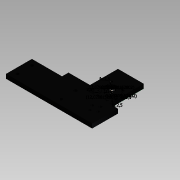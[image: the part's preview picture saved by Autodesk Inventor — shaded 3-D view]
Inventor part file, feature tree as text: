
AUTODESK INVENTOR PART (.ipt)
format: ipt  version: 2015 SP1 (Build 190203100, 203)  size: 229,888 bytes
history: native  units: mm
features: sketch x13, extrude x11, reference x5, other x2, plane x1, sweep x1, projected_geometry x1
ambient origin geometry x8: Origin, YZ Plane, XZ Plane, XY Plane, X Axis, Y Axis, Z Axis, Center Point
bodies: Solid1 (feature_tree)
feature tree (34):
  sketch  "Sketch1"  dims[d0=5.0mm d1=0.0mm d2=100.0mm]
  extrude  "Extrusion1"  Depth=100.0mm
  extrude  "Extrusion3"  Depth=30.0mm TaperAngle=0.0deg
  extrude  "Extrusion4"  Depth=10.0mm
  sketch  "Sketch6"  dims[d9=10.0mm d10=0.0mm d19=0.616194mm]
  sketch  "Sketch7"  dims[d22=30.0mm d23=5.0mm]
  plane  "Work Plane2"
  sweep  "Sweep1"
  other  "YZ 0"
  other  "XY 0"
  extrude  "Extrusion8"  Depth=6.802721mm
  extrude  "Extrusion9"  TaperAngle=90.0deg  [1 undecoded]
  extrude  "Extrusion10"  Depth=25.0mm
  extrude  "Extrusion11"  Depth=6.803mm
  extrude  "Extrusion12"  Depth=10.0mm TaperAngle=0.0deg
  extrude  "Extrusion13"  Depth=10.0mm TaperAngle=0.0deg
  extrude  "Extrusion14"  Depth=15.0mm
  extrude  "Extrusion15"  Depth=10.0mm
  sketch  "Sketch4"  dims[d6=30.0mm d7=3.5mm d8=0.0mm]
  reference  "Reference3"
  reference  "Reference4"
  reference  "Reference5"
  reference  "Reference6"
  reference  "Reference7"
  projected_geometry  "Projected Loop1"
  sketch  "Sketch9"  dims[d24=6.802721mm d25=6.802721mm]
  sketch  "Sketch12"  dims[d26=5.0mm d27=90.0deg]
  sketch  "Sketch13"  dims[d28=25.0mm d29=80.0mm]
  sketch  "Sketch15"  dims[d30=0.0mm d31=0.0mm d32=6.803mm d33=-11.25mm]
  sketch  "Sketch16"  dims[d36=10.0mm d37=0.0mm d38=10.0mm d39=0.0mm]
  sketch  "Sketch17"  dims[d40=9.0mm d41=10.0mm d42=0.0mm]
  sketch  "Sketch18"  dims[d43=15.0mm d44=15.0mm]
  sketch  "Sketch19"  dims[d45=10.0mm d46=0.0mm d47=3.0mm]
  sketch  "Sketch20"  dims[d48=3.0mm d49=3.0mm d50=3.0mm d51=3.315mm d52=3.315mm d53=7.071068mm d54=7.071068mm d55=7.071068mm d56=7.071068mm d57=0.0mm d64=12.020815mm d65=12.020815mm d66=12.020815mm d67=12.020815mm d68=17.0mm d69=17.0mm d70=2.5mm d71=2.5mm d72=2.5mm d73=2.5mm d74=10.0mm d75=0.0mm d76=10.0mm d77=30.0mm d78=0.0mm d79=10.0mm d80=2.5mm d81=0.0mm d82=45.0deg d83=30.0mm d84=0.0mm d85=5.0mm d86=0.0mm]
note: 1 required parameter value undecoded (feature->parameter linkage not recoverable at this tier; creation-order binding heuristic only, values carry confidence <= 0.55)
